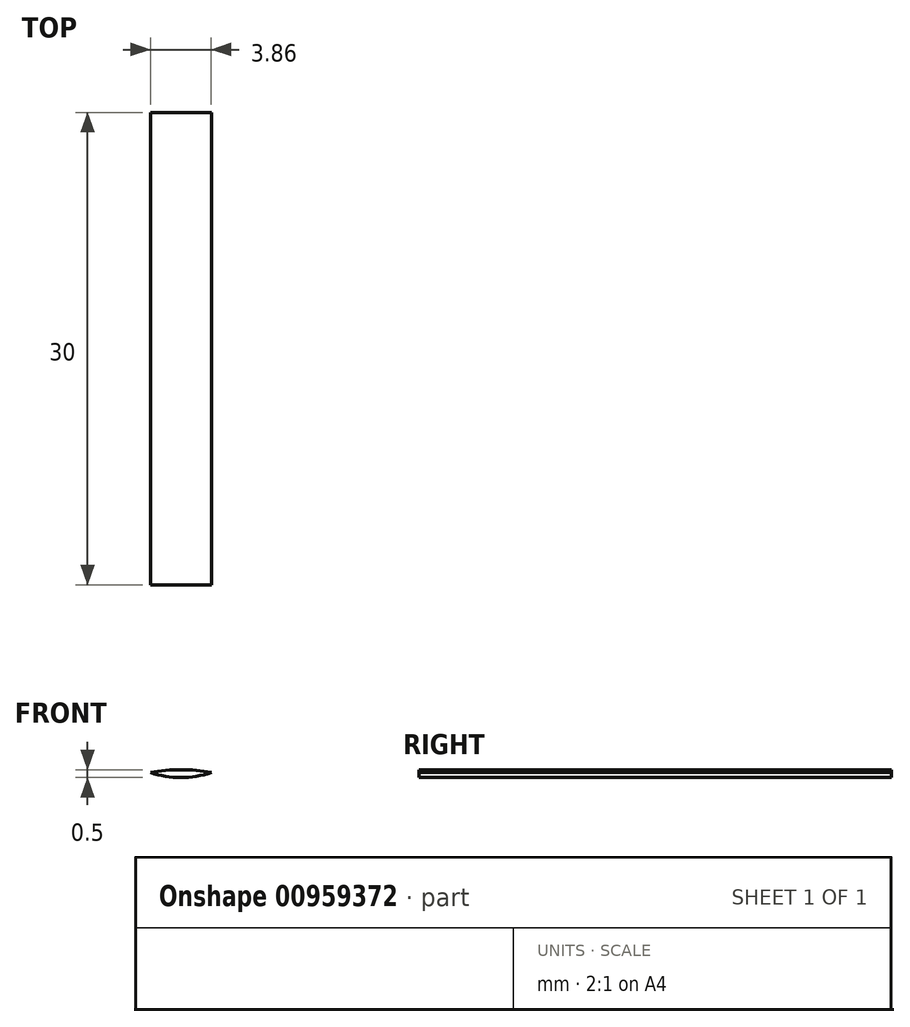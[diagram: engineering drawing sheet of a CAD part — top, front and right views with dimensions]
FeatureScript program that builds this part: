
annotation { "Feature Type Name" : "Feature", "Feature Type Description" : "" }
export const myFeature = defineFeature(function(context is Context, id is Id, definition is map)
    precondition{}
    {
        {
            var Q0;
            Q0=qCreatedBy(makeId("Front.planeOp"),FACE);
            var sketch = newSketch(context, id + "F0", { "sketchPlane" : qUnion([Q0])});
            skCircle(sketch, "E0", {"center": v(0, 0) * mm, "radius": 10.5 * mm});
            skCircle(sketch, "E1", {"center": v(0, 0) * mm, "radius": 12 * mm});
            skCircle(sketch, "E2", {"center": v(0, 16) * mm, "radius": 2.5 * mm});
            skCircle(sketch, "E3", {"center": v(0, 16) * mm, "radius": 6 * mm});
            skLineSegment(sketch, "E4", {"start": v(-5.56, 18.25) * mm, "end": v(-11.12, 4.5) * mm});
            skLineSegment(sketch, "E5", {"start": v(5.56, 18.25) * mm, "end": v(11.12, 4.5) * mm});
            skCircle(sketch, "E6", {"center": v(0, 0) * mm, "radius": 6 * mm});
            skSolve(sketch);
        }
        {
            var Q0;
            {var subQ0=sQuery(id+"F0.wireOp",EDGE,"E3");var subQ1=sQuery(id+"F0.wireOp",EDGE,"E0");var subQ2=makeQuery(id+"F0.imprint","INTERSECT",VERTEX,{"disambiguationData":[OD(0.0)],"derivedFrom":[subQ1,subQ0]});Q0=makeQuery(id+"F0.imprint","IMPRINT",FACE,{"disambiguationData":[TD([[makeQuery(id+"F0.imprint","IMPRINT",EDGE,{"disambiguationData":[TD([[subQ2,-1.0]])],"derivedFrom":subQ1}),1.0]])]});}
            extrude(context, id + "F1", {"entities" : qUnion([Q0]), "depth" : 30 * mm, "offsetDistance" : 25 * mm});
        }
    });
